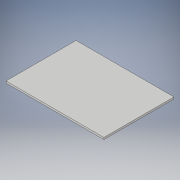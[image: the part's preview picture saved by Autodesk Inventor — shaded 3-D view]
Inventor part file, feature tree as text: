
AUTODESK INVENTOR PART (.ipt)
format: ipt  version: 2018.2 (Build 222227000, 227)  size: 90,624 bytes
history: native  units: in
note: dims shown in document units (in); Inventor stores cm internally (conversion verified against a paired STEP export)
features: extrude x1, sketch x1
ambient origin geometry x8: Origin, YZ Plane, XZ Plane, XY Plane, X Axis, Y Axis, Z Axis, Center Point
bodies: Solid1 (feature_tree)
feature tree (2):
  extrude  "Extrusion1"  Depth=0.75in
  sketch  "Sketch1"  dims[d0=39.398in d1=0.75in d2=28.228in d3=0.0in]
